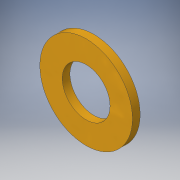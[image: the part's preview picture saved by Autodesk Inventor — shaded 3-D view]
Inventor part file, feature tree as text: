
AUTODESK INVENTOR PART (.ipt)
format: ipt  version: 2016 (Build 200138000, 138)  size: 100,352 bytes
history: native  units: in
note: dims shown in document units (in); Inventor stores cm internally (conversion verified against a paired STEP export)
features: extrude x1, sketch x1
ambient origin geometry x8: Origin, YZ Plane, XZ Plane, XY Plane, X Axis, Y Axis, Z Axis, Center Point
bodies: Solid1 (feature_tree)
feature tree (2):
  extrude  "Extrusion1"  Depth=0.0197in
  sketch  "Sketch1"  dims[d0=0.2362in d1=0.122in d2=0.0197in d3=0.0in]
